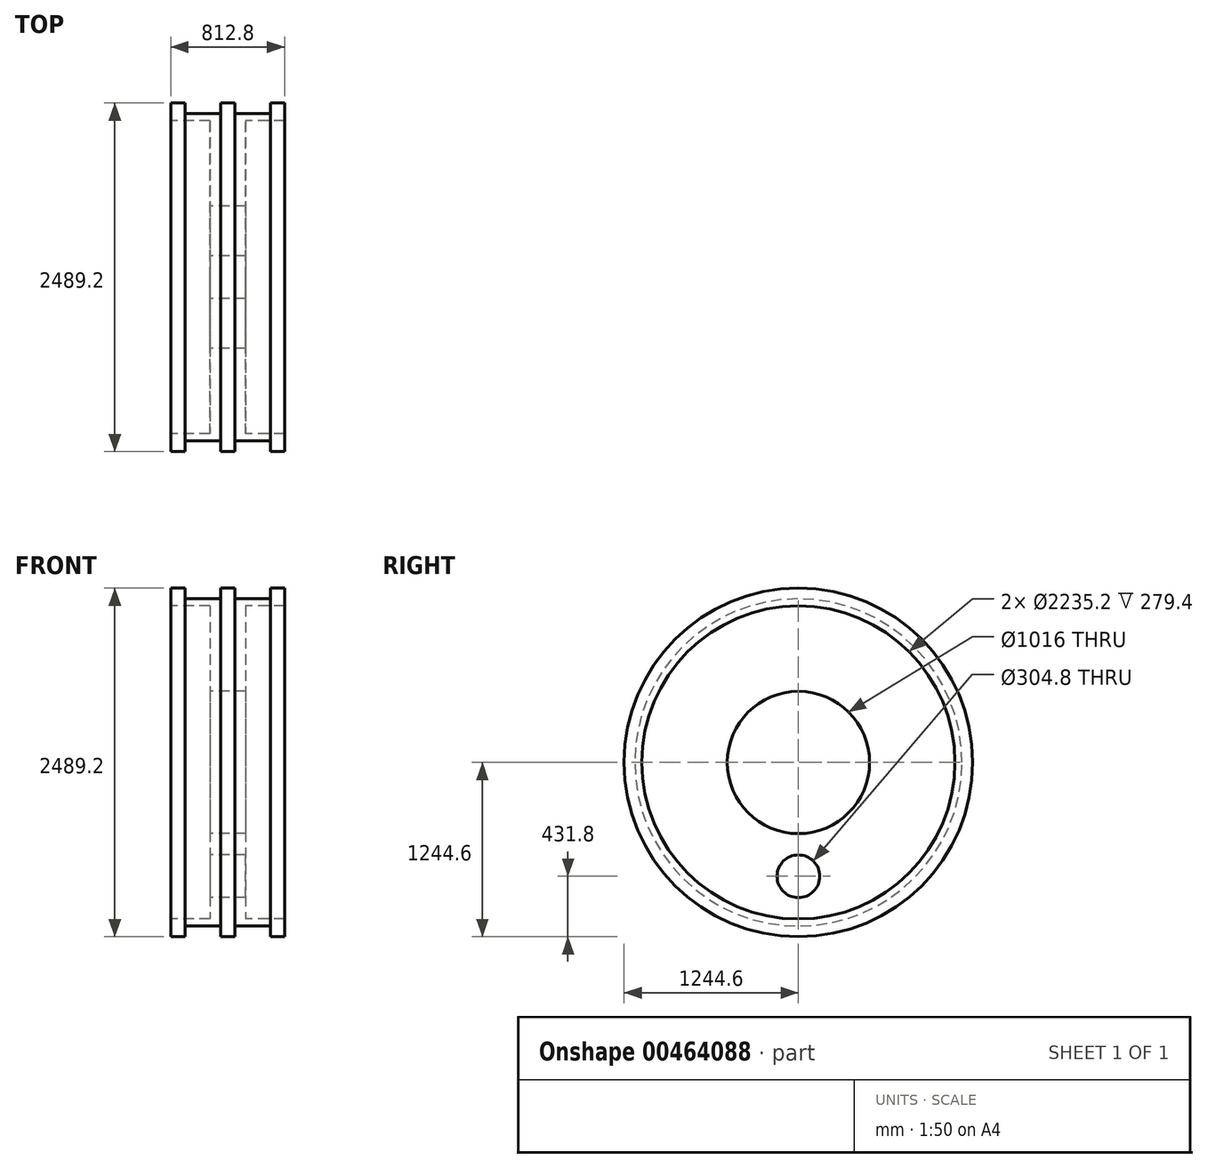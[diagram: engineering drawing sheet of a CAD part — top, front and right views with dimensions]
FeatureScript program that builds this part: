
annotation { "Feature Type Name" : "Feature", "Feature Type Description" : "" }
export const myFeature = defineFeature(function(context is Context, id is Id, definition is map)
    precondition{}
    {
        {
            var Q0;
            Q0=qCreatedBy(makeId("Front.planeOp"),FACE);
            var sketch = newSketch(context, id + "F0", { "sketchPlane" : qUnion([Q0])});
            skLineSegment(sketch, "E0", {"start": v(-127, 0) * mm, "end": v(-406.4, 0) * mm});
            skLineSegment(sketch, "E1", {"start": v(-406.4, 0) * mm, "end": v(-127, 0) * mm});
            skLineSegment(sketch, "E2", {"start": v(-127, -609.6) * mm, "end": v(-127, 0) * mm});
            skLineSegment(sketch, "E3.MirrorCS", {"start": v(406.4, 0) * mm, "end": v(127, 0) * mm});
            skLineSegment(sketch, "E4.MirrorCS", {"start": v(127, -609.6) * mm, "end": v(127, 0) * mm});
            skLineSegment(sketch, "E5", {"start": v(-406.4, -609.6) * mm, "end": v(-127, -609.6) * mm});
            skLineSegment(sketch, "E6", {"start": v(-406.4, -609.6) * mm, "end": v(-406.4, -736.6) * mm});
            skLineSegment(sketch, "E7", {"start": v(406.4, -609.6) * mm, "end": v(406.4, -736.6) * mm});
            skLineSegment(sketch, "E8", {"start": v(-406.4, -736.6) * mm, "end": v(-304.8, -736.6) * mm});
            skLineSegment(sketch, "E9", {"start": v(-304.8, -736.6) * mm, "end": v(-304.8, -660.4) * mm});
            skLineSegment(sketch, "E10", {"start": v(406.4, -736.6) * mm, "end": v(304.8, -736.6) * mm});
            skLineSegment(sketch, "E11", {"start": v(304.8, -736.6) * mm, "end": v(304.8, -660.4) * mm});
            skLineSegment(sketch, "E12.bottom", {"start": v(-50.8, -736.6) * mm, "end": v(50.8, -736.6) * mm});
            skPoint(sketch, "E12.middle", {"position": v(0, -609.6) * mm});
            skPoint(sketch, "E12.top.end.orphan", {"position": v(50.8, -482.6) * mm});
            skPoint(sketch, "E12.top.start.orphan", {"position": v(-50.8, -482.6) * mm});
            skLineSegment(sketch, "E13", {"start": v(-304.8, -660.4) * mm, "end": v(-50.8, -660.4) * mm});
            skLineSegment(sketch, "E14", {"start": v(-50.8, -660.4) * mm, "end": v(-50.8, -736.6) * mm});
            skLineSegment(sketch, "E15", {"start": v(304.8, -660.4) * mm, "end": v(50.8, -660.4) * mm});
            skLineSegment(sketch, "E16", {"start": v(50.8, -660.4) * mm, "end": v(50.8, -736.6) * mm});
            skLineSegment(sketch, "E17", {"start": v(-406.4, 0) * mm, "end": v(-406.4, 152.4) * mm});
            skLineSegment(sketch, "E18", {"start": v(-406.4, 152.4) * mm, "end": v(406.4, 152.4) * mm});
            skLineSegment(sketch, "E19", {"start": v(406.4, 152.4) * mm, "end": v(406.4, 0) * mm});
            skPoint(sketch, "E20.orphan", {"position": v(0, 0) * mm});
            skLineSegment(sketch, "E21.trimOffspring", {"start": v(127, -609.6) * mm, "end": v(406.4, -609.6) * mm});
            skLineSegment(sketch, "E22", {"start": v(-127, 0) * mm, "end": v(127, 0) * mm});
            skLineSegment(sketch, "E23", {"start": v(0, 152.4) * mm, "end": v(0, 508) * mm});
            skPoint(sketch, "E23.endSnap0", {"position": v(0, 152.4) * mm});
            skLineSegment(sketch, "E24", {"start": v(-406.4, 508) * mm, "end": v(406.4, 508) * mm});
            skSolve(sketch);
        }
        {
            var Q0;
            Q0=makeQuery(id+"F0.imprint","IMPRINT",FACE,{"disambiguationData":[TD([[makeQuery(id+"F0.imprint","IMPRINT",EDGE,{"derivedFrom":sQuery(id+"F0.wireOp",EDGE,"E2")}),-1.0]])]});
            var Q1;
            Q1=makeQuery(id+"F0.imprint","IMPRINT",FACE,{"disambiguationData":[TD([[makeQuery(id+"F0.imprint","IMPRINT",EDGE,{"derivedFrom":sQuery(id+"F0.wireOp",EDGE,"E1")}),1.0]])]});
            var Q2;
            Q2=sQuery(id+"F0.wireOp",EDGE,"E24");
            revolve(context, id + "F1", {"entities" : qUnion([Q0, Q1]), "axis" : qUnion([Q2]), "revolveType" : RevolveType.FULL});
        }
        {
            var Q0;
            Q0=makeQuery(id+"F1.opRevolve","SWEPT_FACE",FACE,{"disambiguationData":[OSD([sQuery(id+"F0.wireOp",EDGE,"E2")])]});
            var sketch = newSketch(context, id + "F2", { "sketchPlane" : qUnion([Q0])});
            skLineSegment(sketch, "E25", {"start": v(0, 0) * mm, "end": v(0, -304.8) * mm});
            skCircle(sketch, "E26", {"center": v(0, -304.8) * mm, "radius": 152.4 * mm});
            skSolve(sketch);
        }
        {
            var Q0;
            Q0=makeQuery(id+"F7NzlZnnyP0G74T_1.6.F2.imprint","IMPRINT",FACE,{"disambiguationData":[TD([[makeQuery(id+"F7NzlZnnyP0G74T_1.6.F2.imprint","IMPRINT",EDGE,{"derivedFrom":sQuery(id+"F7NzlZnnyP0G74T_1.6.F2.wireOp",EDGE,"E26")}),1.0]])]});
            var Q1;
            Q1=makeQuery(id+"F7NzlZnnyP0G74T_1.5.F2.imprint","IMPRINT",FACE,{"disambiguationData":[TD([[makeQuery(id+"F7NzlZnnyP0G74T_1.5.F2.imprint","IMPRINT",EDGE,{"derivedFrom":sQuery(id+"F7NzlZnnyP0G74T_1.5.F2.wireOp",EDGE,"E26")}),1.0]])]});
            var Q2;
            Q2=makeQuery(id+"F7NzlZnnyP0G74T_1.4.F2.imprint","IMPRINT",FACE,{"disambiguationData":[TD([[makeQuery(id+"F7NzlZnnyP0G74T_1.4.F2.imprint","IMPRINT",EDGE,{"derivedFrom":sQuery(id+"F7NzlZnnyP0G74T_1.4.F2.wireOp",EDGE,"E26")}),1.0]])]});
            var Q3;
            Q3=makeQuery(id+"F7NzlZnnyP0G74T_1.3.F2.imprint","IMPRINT",FACE,{"disambiguationData":[TD([[makeQuery(id+"F7NzlZnnyP0G74T_1.3.F2.imprint","IMPRINT",EDGE,{"derivedFrom":sQuery(id+"F7NzlZnnyP0G74T_1.3.F2.wireOp",EDGE,"E26")}),1.0]])]});
            var Q4;
            Q4=makeQuery(id+"F7NzlZnnyP0G74T_1.2.F2.imprint","IMPRINT",FACE,{"disambiguationData":[TD([[makeQuery(id+"F7NzlZnnyP0G74T_1.2.F2.imprint","IMPRINT",EDGE,{"derivedFrom":sQuery(id+"F7NzlZnnyP0G74T_1.2.F2.wireOp",EDGE,"E26")}),1.0]])]});
            var Q5;
            Q5=makeQuery(id+"F7NzlZnnyP0G74T_1.1.F2.imprint","IMPRINT",FACE,{"disambiguationData":[TD([[makeQuery(id+"F7NzlZnnyP0G74T_1.1.F2.imprint","IMPRINT",EDGE,{"derivedFrom":sQuery(id+"F7NzlZnnyP0G74T_1.1.F2.wireOp",EDGE,"E26")}),1.0]])]});
            var Q6;
            Q6=makeQuery(id+"F2.imprint","IMPRINT",FACE,{"disambiguationData":[TD([[makeQuery(id+"F2.imprint","IMPRINT",EDGE,{"derivedFrom":sQuery(id+"F2.wireOp",EDGE,"E26")}),1.0]])]});
            extrude(context, id + "F3", {"entities" : qUnion([Q0, Q1, Q2, Q3, Q4, Q5, Q6]), "operationType" : NewBodyOperationType.REMOVE, "endBound" : BoundingType.THROUGH_ALL, "oppositeDirection" : true, "depth" : 25.4 * mm});
        }
    });
